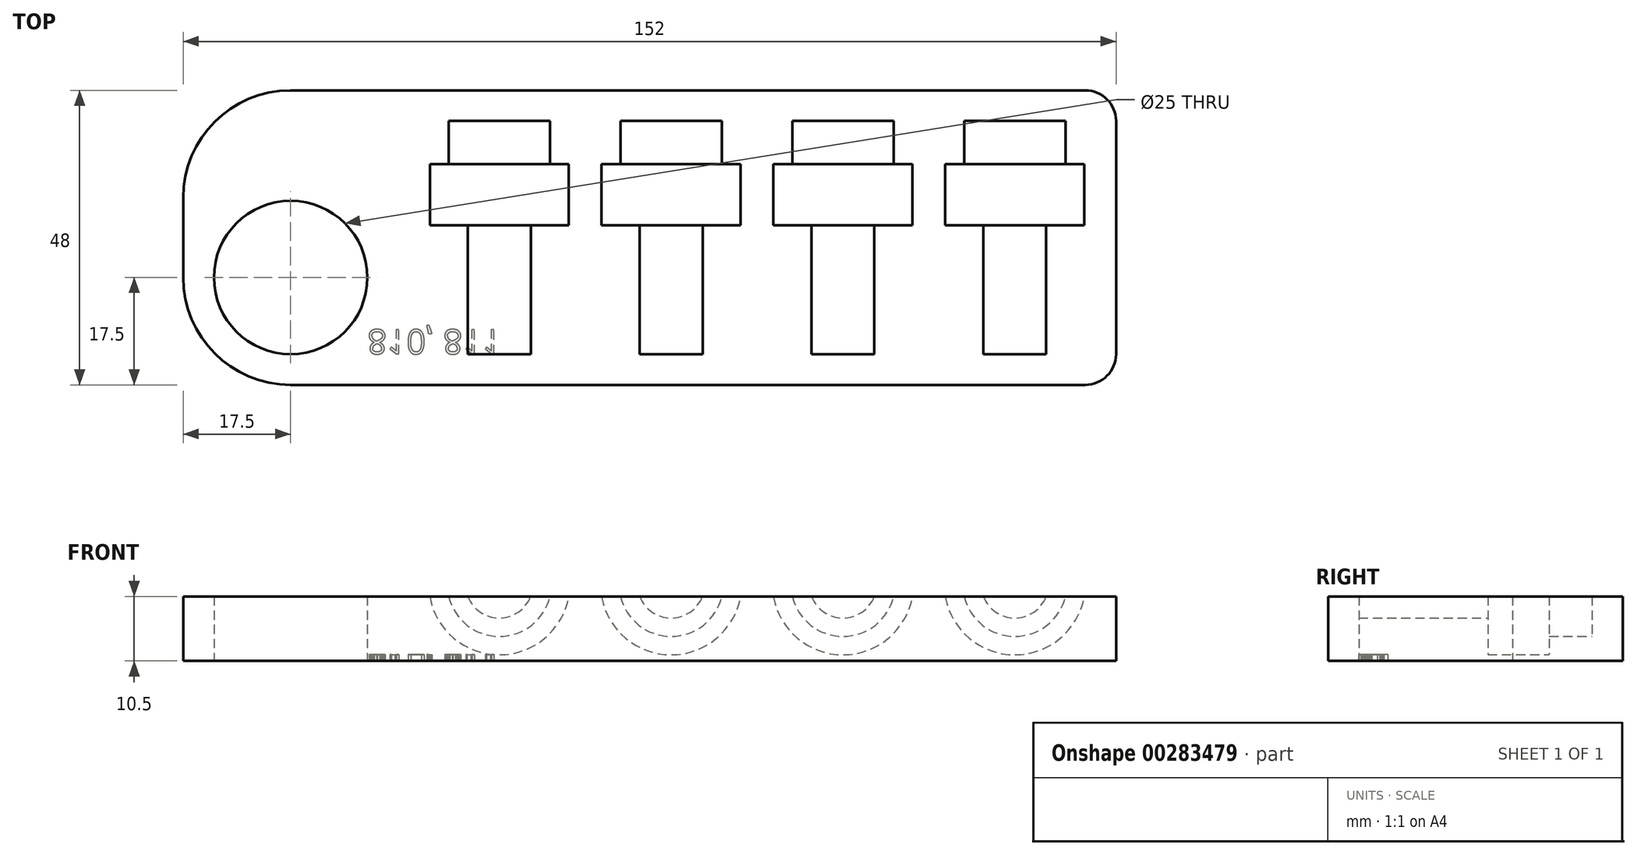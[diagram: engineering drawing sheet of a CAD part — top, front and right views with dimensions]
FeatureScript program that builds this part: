
annotation { "Feature Type Name" : "Feature", "Feature Type Description" : "" }
export const myFeature = defineFeature(function(context is Context, id is Id, definition is map)
    precondition{}
    {
        {
            var Q0;
            Q0=qCreatedBy(makeId("Top.planeOp"),FACE);
            var sketch = newSketch(context, id + "F0", { "sketchPlane" : qUnion([Q0])});
            skLineSegment(sketch, "E0.bottom", {"start": v(17.5, 0) * mm, "end": v(147, 0) * mm});
            skLineSegment(sketch, "E0.top", {"start": v(17.5, 48) * mm, "end": v(147, 48) * mm});
            skLineSegment(sketch, "E0.left", {"start": v(0, 17.5) * mm, "end": v(0, 30.5) * mm});
            skLineSegment(sketch, "E0.right", {"start": v(152, 5) * mm, "end": v(152, 43) * mm});
            skLineSegment(sketch, "E1.bottom", {"start": v(0, 0) * mm, "end": v(17.5, 0) * mm, "construction": true});
            skLineSegment(sketch, "E1.top", {"start": v(0, 17.5) * mm, "end": v(17.5, 17.5) * mm, "construction": true});
            skLineSegment(sketch, "E1.left", {"start": v(0, 0) * mm, "end": v(0, 17.5) * mm, "construction": true});
            skLineSegment(sketch, "E1.right", {"start": v(17.5, 0) * mm, "end": v(17.5, 17.5) * mm, "construction": true});
            skCircle(sketch, "E2", {"center": v(17.5, 17.5) * mm, "radius": 12.5 * mm});
            skPoint(sketch, "E3.visualSharp", {"position": v(0, 0) * mm});
            skArc(sketch, "E3.filletArc", {"start": v(0, 17.5) * mm, "mid": v(5.13, 5.13) * mm, "end": v(17.5, 0) * mm});
            skPoint(sketch, "E4.visualSharp", {"position": v(0, 48) * mm});
            skArc(sketch, "E4.filletArc", {"start": v(17.5, 48) * mm, "mid": v(5.13, 42.87) * mm, "end": v(0, 30.5) * mm});
            skPoint(sketch, "E5.visualSharp", {"position": v(152, 48) * mm});
            skArc(sketch, "E5.filletArc", {"start": v(152, 43) * mm, "mid": v(150.54, 46.54) * mm, "end": v(147, 48) * mm});
            skPoint(sketch, "E6.visualSharp", {"position": v(152, 0) * mm});
            skArc(sketch, "E6.filletArc", {"start": v(147, 0) * mm, "mid": v(150.54, 1.46) * mm, "end": v(152, 5) * mm});
            skSolve(sketch);
        }
        {
            var Q0;
            Q0=makeQuery(id+"F0.imprint","IMPRINT",FACE,{"disambiguationData":[TD([[makeQuery(id+"F0.imprint","IMPRINT",EDGE,{"derivedFrom":sQuery(id+"F0.wireOp",EDGE,"E0.bottom")}),1.0]])]});
            extrude(context, id + "F1", {"entities" : qUnion([Q0]), "depth" : 10.5 * mm});
        }
        {
            var Q0;
            Q0=makeQuery(id+"F1.opExtrude","CAP_FACE",FACE,{"disambiguationData":[OSD([sQuery(id+"F0.wireOp",EDGE,"E0.bottom"),sQuery(id+"F0.wireOp",EDGE,"E0.top"),sQuery(id+"F0.wireOp",EDGE,"E0.right"),sQuery(id+"F0.wireOp",EDGE,"E2"),sQuery(id+"F0.wireOp",EDGE,"E3.filletArc"),sQuery(id+"F0.wireOp",EDGE,"E4.filletArc"),sQuery(id+"F0.wireOp",EDGE,"E5.filletArc"),sQuery(id+"F0.wireOp",EDGE,"E6.filletArc")])],"isStart":false});
            cPlane(context, id + "F2", {"entities" : qUnion([Q0]), "cplaneType" : CPlaneType.OFFSET, "offset" : 2 * mm, "width" : 150 * mm, "height" : 150 * mm});
        }
        {
            var Q0;
            Q0=qCreatedBy(id+"F2.planeOp",FACE);
            var sketch = newSketch(context, id + "F3", { "sketchPlane" : qUnion([Q0])});
            skLineSegment(sketch, "E7.bottom", {"start": v(0, 0) * mm, "end": v(51.5, 0) * mm, "construction": true});
            skLineSegment(sketch, "E7.top", {"start": v(0, 5) * mm, "end": v(51.5, 5) * mm, "construction": true});
            skLineSegment(sketch, "E7.left", {"start": v(0, 0) * mm, "end": v(0, 5) * mm, "construction": true});
            skLineSegment(sketch, "E7.right", {"start": v(51.5, 0) * mm, "end": v(51.5, 5) * mm, "construction": true});
            skLineSegment(sketch, "E8.bottom", {"start": v(51.5, 5) * mm, "end": v(57, 5) * mm});
            skLineSegment(sketch, "E8.left", {"start": v(51.5, 5) * mm, "end": v(51.5, 26) * mm});
            skLineSegment(sketch, "E8.right", {"start": v(57, 5) * mm, "end": v(57, 26) * mm});
            skLineSegment(sketch, "E9.bottom", {"start": v(57, 26) * mm, "end": v(63, 26) * mm});
            skLineSegment(sketch, "E9.top", {"start": v(60, 36) * mm, "end": v(63, 36) * mm});
            skLineSegment(sketch, "E9.left", {"start": v(51.5, 26) * mm, "end": v(51.5, 36) * mm});
            skLineSegment(sketch, "E9.right", {"start": v(63, 26) * mm, "end": v(63, 36) * mm});
            skLineSegment(sketch, "E10.top", {"start": v(51.5, 43) * mm, "end": v(60, 43) * mm});
            skLineSegment(sketch, "E10.left", {"start": v(51.5, 36) * mm, "end": v(51.5, 43) * mm});
            skLineSegment(sketch, "E10.right", {"start": v(60, 36) * mm, "end": v(60, 43) * mm});
            skLineSegment(sketch, "E11", {"start": v(51.5, 5) * mm, "end": v(79.5, 5) * mm, "construction": true});
            skLineSegment(sketch, "E12", {"start": v(79.5, 5) * mm, "end": v(107.5, 5) * mm, "construction": true});
            skLineSegment(sketch, "E13", {"start": v(107.5, 5) * mm, "end": v(135.5, 5) * mm, "construction": true});
            skLineSegment(sketch, "E14.bottom", {"start": v(79.5, 5) * mm, "end": v(85, 5) * mm});
            skLineSegment(sketch, "E14.left", {"start": v(79.5, 5) * mm, "end": v(79.5, 26) * mm});
            skLineSegment(sketch, "E14.right", {"start": v(85, 5) * mm, "end": v(85, 26) * mm});
            skLineSegment(sketch, "E15.bottom", {"start": v(85, 26) * mm, "end": v(91, 26) * mm});
            skLineSegment(sketch, "E15.top", {"start": v(88, 36) * mm, "end": v(91, 36) * mm});
            skLineSegment(sketch, "E15.left", {"start": v(79.5, 26) * mm, "end": v(79.5, 36) * mm});
            skLineSegment(sketch, "E15.right", {"start": v(91, 26) * mm, "end": v(91, 36) * mm});
            skLineSegment(sketch, "E16.top", {"start": v(79.5, 43) * mm, "end": v(88, 43) * mm});
            skLineSegment(sketch, "E16.left", {"start": v(79.5, 36) * mm, "end": v(79.5, 43) * mm});
            skLineSegment(sketch, "E16.right", {"start": v(88, 36) * mm, "end": v(88, 43) * mm});
            skLineSegment(sketch, "E17.bottom", {"start": v(107.5, 5) * mm, "end": v(113, 5) * mm});
            skLineSegment(sketch, "E17.left", {"start": v(107.5, 5) * mm, "end": v(107.5, 26) * mm});
            skLineSegment(sketch, "E17.right", {"start": v(113, 5) * mm, "end": v(113, 26) * mm});
            skLineSegment(sketch, "E18.bottom", {"start": v(113, 26) * mm, "end": v(119, 26) * mm});
            skLineSegment(sketch, "E18.top", {"start": v(116, 36) * mm, "end": v(119, 36) * mm});
            skLineSegment(sketch, "E18.left", {"start": v(107.5, 26) * mm, "end": v(107.5, 36) * mm});
            skLineSegment(sketch, "E18.right", {"start": v(119, 26) * mm, "end": v(119, 36) * mm});
            skLineSegment(sketch, "E19.top", {"start": v(107.5, 43) * mm, "end": v(116, 43) * mm});
            skLineSegment(sketch, "E19.left", {"start": v(107.5, 36) * mm, "end": v(107.5, 43) * mm});
            skLineSegment(sketch, "E19.right", {"start": v(116, 36) * mm, "end": v(116, 43) * mm});
            skLineSegment(sketch, "E20.bottom", {"start": v(135.5, 5) * mm, "end": v(141, 5) * mm});
            skLineSegment(sketch, "E20.left", {"start": v(135.5, 5) * mm, "end": v(135.5, 26) * mm});
            skLineSegment(sketch, "E20.right", {"start": v(141, 5) * mm, "end": v(141, 26) * mm});
            skLineSegment(sketch, "E21.bottom", {"start": v(141, 26) * mm, "end": v(147, 26) * mm});
            skLineSegment(sketch, "E21.top", {"start": v(144, 36) * mm, "end": v(147, 36) * mm});
            skLineSegment(sketch, "E21.left", {"start": v(135.5, 26) * mm, "end": v(135.5, 36) * mm});
            skLineSegment(sketch, "E21.right", {"start": v(147, 26) * mm, "end": v(147, 36) * mm});
            skLineSegment(sketch, "E22.top", {"start": v(135.5, 43) * mm, "end": v(144, 43) * mm});
            skLineSegment(sketch, "E22.left", {"start": v(135.5, 36) * mm, "end": v(135.5, 43) * mm});
            skLineSegment(sketch, "E22.right", {"start": v(144, 36) * mm, "end": v(144, 43) * mm});
            skSolve(sketch);
        }
        {
            var Q0;
            Q0=makeQuery(id+"F3.imprint","IMPRINT",FACE,{"disambiguationData":[TD([[makeQuery(id+"F3.imprint","IMPRINT",EDGE,{"derivedFrom":sQuery(id+"F3.wireOp",EDGE,"E8.bottom")}),1.0]])]});
            var Q1;
            Q1=sQuery(id+"F3.wireOp",EDGE,"E9.left");
            revolve(context, id + "F4", {"operationType" : NewBodyOperationType.REMOVE, "entities" : qUnion([Q0]), "axis" : qUnion([Q1]), "revolveType" : RevolveType.FULL, "oppositeDirection" : true});
        }
        {
            var Q0;
            Q0=makeQuery(id+"F3.imprint","IMPRINT",FACE,{"disambiguationData":[TD([[makeQuery(id+"F3.imprint","IMPRINT",EDGE,{"derivedFrom":sQuery(id+"F3.wireOp",EDGE,"E14.bottom")}),1.0]])]});
            var Q1;
            Q1=sQuery(id+"F3.wireOp",EDGE,"E15.left");
            revolve(context, id + "F5", {"operationType" : NewBodyOperationType.REMOVE, "entities" : qUnion([Q0]), "axis" : qUnion([Q1]), "revolveType" : RevolveType.FULL, "oppositeDirection" : true});
        }
        {
            var Q0;
            Q0=makeQuery(id+"F3.imprint","IMPRINT",FACE,{"disambiguationData":[TD([[makeQuery(id+"F3.imprint","IMPRINT",EDGE,{"derivedFrom":sQuery(id+"F3.wireOp",EDGE,"E17.bottom")}),1.0]])]});
            var Q1;
            Q1=sQuery(id+"F3.wireOp",EDGE,"E18.left");
            revolve(context, id + "F6", {"operationType" : NewBodyOperationType.REMOVE, "entities" : qUnion([Q0]), "axis" : qUnion([Q1]), "revolveType" : RevolveType.FULL, "oppositeDirection" : true});
        }
        {
            var Q0;
            Q0=makeQuery(id+"F3.imprint","IMPRINT",FACE,{"disambiguationData":[TD([[makeQuery(id+"F3.imprint","IMPRINT",EDGE,{"derivedFrom":sQuery(id+"F3.wireOp",EDGE,"E20.bottom")}),1.0]])]});
            var Q1;
            Q1=sQuery(id+"F3.wireOp",EDGE,"E21.left");
            revolve(context, id + "F7", {"operationType" : NewBodyOperationType.REMOVE, "entities" : qUnion([Q0]), "axis" : qUnion([Q1]), "revolveType" : RevolveType.FULL, "oppositeDirection" : true});
        }
        {
            var Q0;
            Q0=makeQuery(id+"F1.opExtrude","CAP_FACE",FACE,{"disambiguationData":[OSD([sQuery(id+"F0.wireOp",EDGE,"E0.bottom"),sQuery(id+"F0.wireOp",EDGE,"E0.top"),sQuery(id+"F0.wireOp",EDGE,"E0.left"),sQuery(id+"F0.wireOp",EDGE,"E0.right"),sQuery(id+"F0.wireOp",EDGE,"E2"),sQuery(id+"F0.wireOp",EDGE,"E3.filletArc"),sQuery(id+"F0.wireOp",EDGE,"E4.filletArc"),sQuery(id+"F0.wireOp",EDGE,"E5.filletArc"),sQuery(id+"F0.wireOp",EDGE,"E6.filletArc")])],"isStart":true});
            var sketch = newSketch(context, id + "F8", { "sketchPlane" : qUnion([Q0])});
            skLineSegment(sketch, "E23.bottom", {"start": v(0, 0) * mm, "end": v(30, 0) * mm, "construction": true});
            skLineSegment(sketch, "E23.top", {"start": v(0, -5) * mm, "end": v(30, -5) * mm, "construction": true});
            skLineSegment(sketch, "E23.left", {"start": v(0, 0) * mm, "end": v(0, -5) * mm, "construction": true});
            skLineSegment(sketch, "E23.right", {"start": v(30, 0) * mm, "end": v(30, -5) * mm, "construction": true});
            skText(sketch, "E24", { "text": "810, 811", "fontName": "OpenSans-Regular.ttf"});
            const initialGuessF8  = {"E24": [0.03, -0.009, 1, 0, 0.004]};
            skSetInitialGuess(sketch, initialGuessF8);
            skSolve(sketch);
        }
        {
            var Q0;
            Q0 = qSketchRegion(id + "F8", true);
            extrude(context, id + "F9", {"entities" : qUnion([Q0]), "operationType" : NewBodyOperationType.REMOVE, "oppositeDirection" : true, "depth" : 1 * mm});
        }
    });
